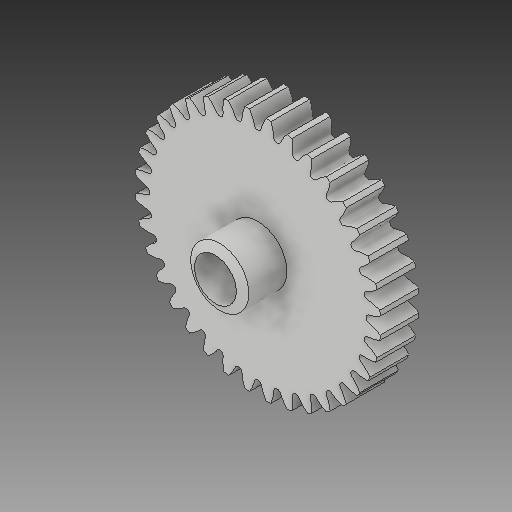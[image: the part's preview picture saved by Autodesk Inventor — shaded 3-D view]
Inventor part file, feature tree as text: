
AUTODESK INVENTOR PART (.ipt)
format: ipt  version: 2017 (Build 210142000, 142)  size: 398,848 bytes
history: native  units: in
note: dims shown in document units (in); Inventor stores cm internally (conversion verified against a paired STEP export)
features: chamfer x1
ambient origin geometry x8: Origin, YZ Plane, XZ Plane, XY Plane, X Axis, Y Axis, Z Axis, Center Point
bodies: Solid1 (feature_tree)
feature tree (1):
  chamfer  "Chamfer1"  [1 undecoded]
note: 1 required parameter value undecoded (feature->parameter linkage not recoverable at this tier; creation-order binding heuristic only, values carry confidence <= 0.55)
